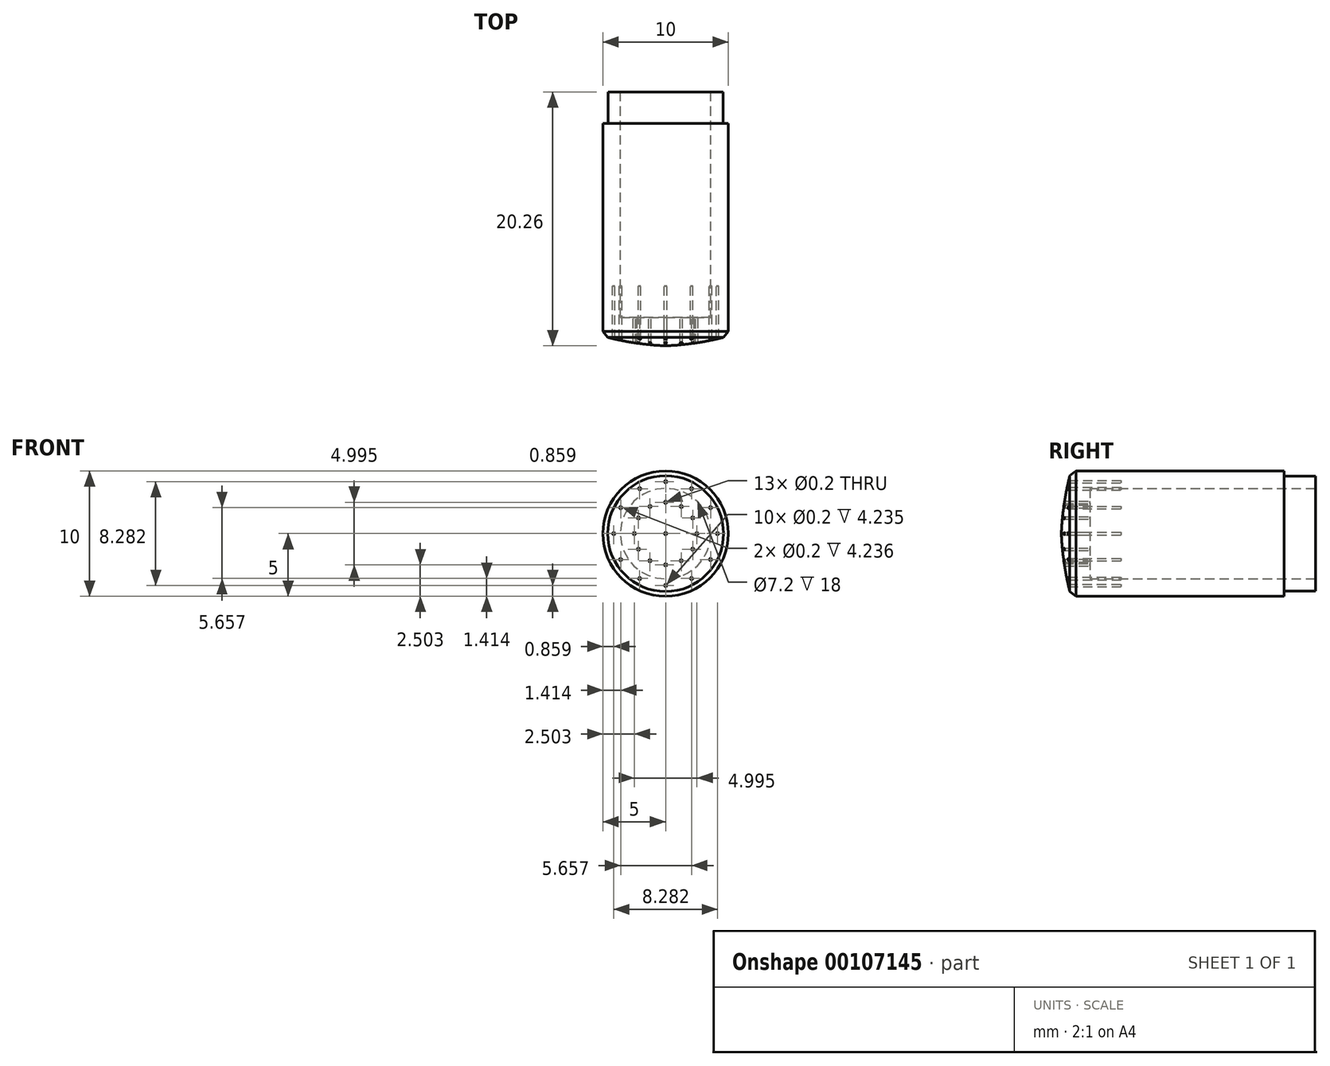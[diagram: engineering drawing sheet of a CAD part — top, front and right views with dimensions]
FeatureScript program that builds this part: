
annotation { "Feature Type Name" : "Feature", "Feature Type Description" : "" }
export const myFeature = defineFeature(function(context is Context, id is Id, definition is map)
    precondition{}
    {
        {
            var Q0;
            Q0=qCreatedBy(makeId("Top.planeOp"),FACE);
            var sketch = newSketch(context, id + "F0", { "sketchPlane" : qUnion([Q0])});
            skLineSegment(sketch, "E0", {"start": v(-50.77, 0) * mm, "end": v(72.32, 0) * mm, "construction": true});
            skLineSegment(sketch, "E1", {"start": v(0, 29.76) * mm, "end": v(0, -21.81) * mm, "construction": true});
            skLineSegment(sketch, "E2", {"start": v(-5, -15.1) * mm, "end": v(-5, 1.9) * mm});
            skLineSegment(sketch, "E3", {"start": v(-5, 1.9) * mm, "end": v(-4.6, 1.9) * mm});
            skLineSegment(sketch, "E4", {"start": v(-4.6, 1.9) * mm, "end": v(-4.6, 4.4) * mm});
            skLineSegment(sketch, "E5", {"start": v(-4.6, 4.4) * mm, "end": v(-3.6, 4.4) * mm});
            skLineSegment(sketch, "E6", {"start": v(-3.6, 4.4) * mm, "end": v(-3.6, -13.6) * mm});
            skLineSegment(sketch, "E7", {"start": v(-3.6, -13.6) * mm, "end": v(0, -13.6) * mm});
            skLineSegment(sketch, "E8", {"start": v(0, -13.6) * mm, "end": v(0, -15.1) * mm});
            skArc(sketch, "E9", {"start": v(-5, -15.1) * mm, "mid": v(-2.52, -15.63) * mm, "end": v(0, -15.87) * mm});
            skLineSegment(sketch, "E10", {"start": v(0, -13.6) * mm, "end": v(0, -15.87) * mm});
            skSolve(sketch);
        }
        {
            var Q0;
            Q0=makeQuery(id+"F0.imprint","IMPRINT",FACE,{"disambiguationData":[TD([[makeQuery(id+"F0.imprint","IMPRINT",EDGE,{"derivedFrom":sQuery(id+"F0.wireOp",EDGE,"E2")}),-1.0]])]});
            var Q1;
            Q1=sQuery(id+"F0.wireOp",EDGE,"E8");
            var Q2;
            Q2=sQuery(id+"F0.wireOp",EDGE,"E7");
            var Q3;
            Q3=sQuery(id+"F0.wireOp",EDGE,"E6");
            var Q4;
            Q4=sQuery(id+"F0.wireOp",EDGE,"E4");
            var Q5;
            Q5=sQuery(id+"F0.wireOp",EDGE,"E2");
            var Q6;
            Q6=sQuery(id+"F0.wireOp",EDGE,"hKVk2ic7-2EHT-0Eln-Ob6q-VbuvlGnT1NPc");
            var Q7;
            Q7=sQuery(id+"F0.wireOp",EDGE,"E5");
            var Q8;
            Q8=sQuery(id+"F0.wireOp",EDGE,"E3");
            var Q9;
            Q9=sQuery(id+"F0.wireOp",EDGE,"E1");
            revolve(context, id + "F1", {"entities" : qUnion([Q0]), "surfaceEntities" : qUnion([Q1, Q2, Q3, Q4, Q5, Q6, Q7, Q8]), "axis" : qUnion([Q9]), "revolveType" : RevolveType.FULL});
        }
        {
            var Q0;
            Q0=makeQuery(id+"F1.opRevolve","SWEPT_EDGE",EDGE,{"disambiguationData":[OSD([sQuery(id+"F0.wireOp",EDGE,"E2"),sQuery(id+"F0.wireOp",EDGE,"E9")])]});
            chamfer(context, id + "F2", {"entities" : qUnion([Q0]), "width" : 0.5 * mm, "tangentPropagation" : true});
        }
        {
            var Q0;
            Q0=qCreatedBy(makeId("Front.planeOp"),FACE);
            var sketch = newSketch(context, id + "F3", { "sketchPlane" : qUnion([Q0])});
            skCircle(sketch, "E11", {"center": v(0, 0) * mm, "radius": 4.14 * mm, "construction": true});
            skCircle(sketch, "E12", {"center": v(0, 0) * mm, "radius": 2.5 * mm, "construction": true});
            skPoint(sketch, "E13", {"position": v(0, 4.14) * mm});
            skPoint(sketch, "E14", {"position": v(0, 2.5) * mm});
            skLineSegment(sketch, "E15.anchor1", {"start": v(0, 0) * mm, "end": v(0, 2.5) * mm, "construction": true});
            skLineSegment(sketch, "E15.anchor2", {"start": v(0, 0) * mm, "end": v(0, 2.5) * mm, "construction": true});
            skPoint(sketch, "E16.1.0", {"position": v(-2.07, 3.59) * mm});
            skPoint(sketch, "E16.2.0", {"position": v(-3.59, 2.07) * mm});
            skPoint(sketch, "E17.0.3.0", {"position": v(-4.14, 0) * mm});
            skPoint(sketch, "E17.0.4.0", {"position": v(-3.59, -2.07) * mm});
            skPoint(sketch, "E17.0.5.0", {"position": v(-2.07, -3.59) * mm});
            skPoint(sketch, "E17.0.6.0", {"position": v(0, -4.14) * mm});
            skPoint(sketch, "E17.0.7.0", {"position": v(2.07, -3.59) * mm});
            skPoint(sketch, "E17.0.8.0", {"position": v(3.59, -2.07) * mm});
            skPoint(sketch, "E17.0.9.0", {"position": v(4.14, 0) * mm});
            skPoint(sketch, "E17.0.10.0", {"position": v(3.59, 2.07) * mm});
            skPoint(sketch, "E17.0.11.0", {"position": v(2.07, 3.59) * mm});
            skPoint(sketch, "E18.1.0", {"position": v(-1.25, 2.16) * mm});
            skPoint(sketch, "E18.2.0", {"position": v(-2.16, 1.25) * mm});
            skPoint(sketch, "E19.0.3.0", {"position": v(-2.5, 0) * mm});
            skPoint(sketch, "E19.0.4.0", {"position": v(-2.16, -1.25) * mm});
            skPoint(sketch, "E19.0.5.0", {"position": v(-1.25, -2.16) * mm});
            skPoint(sketch, "E19.0.6.0", {"position": v(0, -2.5) * mm});
            skPoint(sketch, "E19.0.7.0", {"position": v(1.25, -2.16) * mm});
            skPoint(sketch, "E19.0.8.0", {"position": v(2.16, -1.25) * mm});
            skPoint(sketch, "E19.0.9.0", {"position": v(2.5, 0) * mm});
            skPoint(sketch, "E19.0.10.0", {"position": v(2.16, 1.25) * mm});
            skPoint(sketch, "E19.0.11.0", {"position": v(1.25, 2.16) * mm});
            skSolve(sketch);
        }
        {
            var Q0;
            Q0=makeQuery(id+"F1.opRevolve","SWEPT_BODY",BODY,{"disambiguationData":[OSD([sQuery(id+"F0.wireOp",EDGE,"E2"),sQuery(id+"F0.wireOp",EDGE,"E3"),sQuery(id+"F0.wireOp",EDGE,"E4"),sQuery(id+"F0.wireOp",EDGE,"E5"),sQuery(id+"F0.wireOp",EDGE,"E6"),sQuery(id+"F0.wireOp",EDGE,"E7"),sQuery(id+"F0.wireOp",EDGE,"E9"),sQuery(id+"F0.wireOp",EDGE,"E10")])]});
            transform(context, id + "F4", {"entities" : qUnion([Q0]), "transformType" : TransformType.TRANSLATION_3D, "dx" : 0 * mm, "dy" : 11.1 * mm, "dz" : 0 * mm, "makeCopy" : false});
        }
        {
            var Q0;
            Q0=sQuery(id+"F3.wireOp",VERTEX,"E19.0.9.0");
            var Q1;
            Q1=sQuery(id+"F3.wireOp",VERTEX,"E17.0.5.0");
            var Q2;
            Q2=sQuery(id+"F3.wireOp",VERTEX,"E19.0.7.0");
            var Q3;
            Q3=sQuery(id+"F3.wireOp",VERTEX,"E17.0.3.0");
            var Q4;
            Q4=sQuery(id+"F3.wireOp",VERTEX,"E19.0.5.0");
            var Q5;
            Q5=sQuery(id+"F3.wireOp",VERTEX,"E16.2.0");
            var Q6;
            Q6=sQuery(id+"F3.wireOp",VERTEX,"E18.1.0");
            var Q7;
            Q7=sQuery(id+"F3.wireOp",VERTEX,"E17.0.10.0");
            var Q8;
            Q8=sQuery(id+"F3.wireOp",VERTEX,"E17.0.8.0");
            var Q9;
            Q9=sQuery(id+"F3.wireOp",VERTEX,"E19.0.3.0");
            var Q10;
            Q10=sQuery(id+"F3.wireOp",VERTEX,"E19.0.10.0");
            var Q11;
            Q11=sQuery(id+"F3.wireOp",VERTEX,"E17.0.6.0");
            var Q12;
            Q12=sQuery(id+"F3.wireOp",VERTEX,"E18.2.0");
            var Q13;
            Q13=sQuery(id+"F3.wireOp",VERTEX,"E19.0.8.0");
            var Q14;
            Q14=sQuery(id+"F3.wireOp",VERTEX,"E17.0.4.0");
            var Q15;
            Q15=sQuery(id+"F3.wireOp",VERTEX,"E19.0.6.0");
            var Q16;
            Q16=sQuery(id+"F3.wireOp",VERTEX,"E19.0.11.0");
            var Q17;
            Q17=sQuery(id+"F3.wireOp",VERTEX,"E19.0.4.0");
            var Q18;
            Q18=sQuery(id+"F3.wireOp",VERTEX,"E16.1.0");
            var Q19;
            Q19=sQuery(id+"F3.wireOp",VERTEX,"E17.0.11.0");
            var Q20;
            Q20=sQuery(id+"F3.wireOp",VERTEX,"E11.center");
            var Q21;
            Q21=sQuery(id+"F3.wireOp",VERTEX,"E17.0.9.0");
            var Q22;
            Q22=sQuery(id+"F3.wireOp",VERTEX,"E14");
            var Q23;
            Q23=sQuery(id+"F3.wireOp",VERTEX,"E17.0.7.0");
            var Q24;
            Q24=sQuery(id+"F3.wireOp",VERTEX,"E13");
            var Q25;
            Q25=makeQuery(id+"F1.opRevolve","SWEPT_BODY",BODY,{"disambiguationData":[OSD([sQuery(id+"F0.wireOp",EDGE,"E2"),sQuery(id+"F0.wireOp",EDGE,"E3"),sQuery(id+"F0.wireOp",EDGE,"E4"),sQuery(id+"F0.wireOp",EDGE,"E5"),sQuery(id+"F0.wireOp",EDGE,"E6"),sQuery(id+"F0.wireOp",EDGE,"E7"),sQuery(id+"F0.wireOp",EDGE,"E9"),sQuery(id+"F0.wireOp",EDGE,"E10")])]});
            hole(context, id + "F5", {"style" : HoleStyle.C_BORE, "endStyle" : HoleEndStyle.THROUGH, "oppositeDirection" : true, "holeDiameter" : 0.2 * mm, "cBoreDiameter" : 0.7 * mm, "cBoreDepth" : 0 * mm, "startFromSketch" : true, "locations" : qUnion([Q0, Q1, Q2, Q3, Q4, Q5, Q6, Q7, Q8, Q9, Q10, Q11, Q12, Q13, Q14, Q15, Q16, Q17, Q18, Q19, Q20, Q21, Q22, Q23, Q24]), "scope" : qUnion([Q25]), "isTappedThrough" : true});
        }
    });
